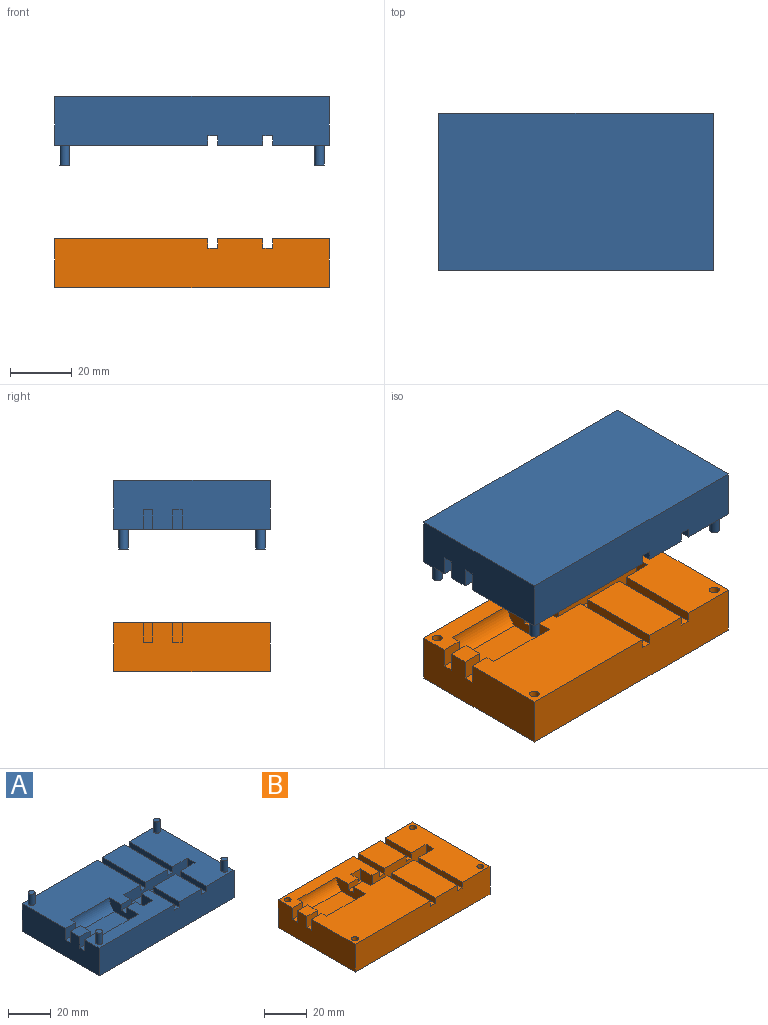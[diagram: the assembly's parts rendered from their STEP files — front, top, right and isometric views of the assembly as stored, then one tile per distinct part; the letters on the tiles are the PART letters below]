
ASSEMBLY  parts=2 mates=1
PART A: 54 faces, bbox 88.9x50.8x22.2 mm
  f0: plane 28.58x14.61mm, normal (0,0,1), area 417.3mm2, adj f9,f18,f34,f36
  f1: plane 17.15x14.61mm, normal (0,0,1), area 250.4mm2, adj f5,f6,f30,f40
  f2: plane 50.8x18.34mm, normal (0,0,1), area 866mm2, adj f5,f6,f9,f18,f29,f37,f39,f44
  f3: plane 49.61x17.15mm, normal (0,0,1), area 450.8mm2, adj f5,f6,f7,f12,f13,f14,f16,f17
  f4: plane 49.61x33.34mm, normal (0,0,1), area 1359.5mm2, adj f9,f12,f14,f15,f16,f18,f20,f23
  f5: plane 88.9x15.88mm, normal (0,-1,0), area 1391.1mm2, adj f1,f2,f3,f14,f29,f30,f31,f32
  f6: plane 35.56x12.7mm, normal (0,1,0), area 350.8mm2, adj f1,f2,f3,f7,f28,f30,f31,f32
  f7: plane 7.62x6.35mm, normal (-1,0,0), area 48.4mm2, adj f3,f6,f17,f28
  f8: plane 6.35x3.18mm, normal (0,0,1), area 20.2mm2, adj f12,f16,f25,f26
  f9: plane 88.9x15.88mm, normal (0,1,0), area 1391.1mm2, adj f0,f2,f4,f14,f29,f33,f34,f35
  f10: plane 6.74x6.35mm, normal (0,1,0), area 42.8mm2, adj f14,f19,f22,f27
  f11: plane 6.74x6.35mm, normal (0,-1,0), area 42.8mm2, adj f14,f19,f22,f27
  f12: plane 19.03x6.35mm, normal (-1,0,0), area 98.7mm2, adj f3,f4,f8,f20,f21,f22,f25,f26
  f13: plane 6.35x3.17mm, normal (1,0,0), area 14mm2, adj f3,f21,f24
  f14: plane 50.8x15.88mm, normal (-1,0,0), area 766.1mm2, adj f3,f4,f5,f9,f10,f11,f22,f23
  f15: plane 6.35x3.17mm, normal (1,0,0), area 14mm2, adj f4,f20,f23
  f16: plane 12.7x6.35mm, normal (1,0,0), area 70.6mm2, adj f3,f4,f8,f17,f18,f25,f26,f28
  f17: plane 6.35x6.35mm, normal (0,1,0), area 40.3mm2, adj f3,f7,f16,f28
  f18: plane 41.91x12.7mm, normal (0,-1,0), area 391.1mm2, adj f0,f2,f4,f16,f28,f33,f34,f35
  f19: plane 6.35x6.35mm, normal (1,0,0), area 40.3mm2, adj f10,f11,f22,f27
  f20: cylinder r=7.95mm len=25.4mm, axis (-1,0,0), area 186.8mm2, adj f4,f12,f15,f22
  f21: cylinder r=7.95mm len=25.4mm, axis (-1,0,0), area 186.8mm2, adj f3,f12,f13,f22
  f22: plane 32.14x12.7mm, normal (0,0,1), area 365.4mm2, adj f10,f11,f12,f14,f19,f20,f21,f23
  f23: plane 6.74x6.35mm, normal (0,-1,0), area 42.8mm2, adj f4,f14,f15,f22
  f24: plane 6.74x6.35mm, normal (0,1,0), area 42.8mm2, adj f3,f13,f14,f22
  f25: plane 6.35x3.18mm, normal (0,1,0), area 20.2mm2, adj f3,f8,f12,f16
  f26: plane 6.35x3.18mm, normal (0,-1,0), area 20.2mm2, adj f4,f8,f12,f16
  f27: plane 6.74x6.35mm, normal (0,0,1), area 42.8mm2, adj f10,f11,f14,f19
  f28: plane 19.05x12.7mm, normal (0,0,1), area 145.2mm2, adj f6,f7,f16,f17,f18,f43
  f29: plane 50.8x15.88mm, normal (1,0,0), area 806.5mm2, adj f2,f5,f9,f42
  f30: plane 17.15x3.18mm, normal (-1,0,0), area 54.4mm2, adj f1,f5,f6,f32
  f31: plane 17.15x3.18mm, normal (1,0,0), area 54.4mm2, adj f3,f5,f6,f32
  f32: plane 17.15x3.18mm, normal (0,0,1), area 54.4mm2, adj f5,f6,f30,f31
  f33: plane 28.58x3.18mm, normal (1,0,0), area 90.7mm2, adj f4,f9,f18,f35
  f34: plane 28.58x3.18mm, normal (-1,0,0), area 90.7mm2, adj f0,f9,f18,f35
  f35: plane 28.58x3.18mm, normal (0,0,1), area 90.7mm2, adj f9,f18,f33,f34
  f36: plane 28.58x3.18mm, normal (1,0,0), area 90.7mm2, adj f0,f9,f18,f38
  f37: plane 28.58x3.18mm, normal (-1,0,0), area 90.7mm2, adj f2,f9,f18,f38
  f38: plane 28.58x3.18mm, normal (0,0,1), area 90.7mm2, adj f9,f18,f36,f37
  f39: plane 17.15x3.18mm, normal (-1,0,0), area 54.4mm2, adj f2,f5,f6,f41
  f40: plane 17.15x3.18mm, normal (1,0,0), area 54.4mm2, adj f1,f5,f6,f41
  f41: plane 17.15x3.18mm, normal (0,0,1), area 54.4mm2, adj f5,f6,f39,f40
  f42: plane 88.9x50.8mm, normal (0,0,-1), area 4516.1mm2, adj f5,f9,f14,f29
  f43: plane 6.35x5.08mm, normal (1,0,0), area 32.3mm2, adj f6,f18,f28,f45
  f44: plane 12.7x5.08mm, normal (-1,0,0), area 64.5mm2, adj f2,f6,f18,f45
  f45: plane 22.86x5.08mm, normal (0,0,1), area 116.1mm2, adj f6,f18,f43,f44
  f46: cylinder r=1.57mm len=6.35mm, axis (0,0,-1), area 62.8mm2, adj f3,f47
  f47: plane 3.15x3.15mm, normal (0,0,1), area 7.8mm2, adj f46
  f48: cylinder r=1.57mm len=6.35mm, axis (0,0,-1), area 62.8mm2, adj f4,f49
  f49: plane 3.15x3.15mm, normal (0,0,1), area 7.8mm2, adj f48
  f50: cylinder r=1.57mm len=6.35mm, axis (0,0,-1), area 62.8mm2, adj f2,f51
  f51: plane 3.15x3.15mm, normal (0,0,1), area 7.8mm2, adj f50
  f52: cylinder r=1.57mm len=6.35mm, axis (0,0,-1), area 62.8mm2, adj f2,f53
  f53: plane 3.15x3.15mm, normal (0,0,1), area 7.8mm2, adj f52
PART B: 54 faces, bbox 88.9x50.8x15.9 mm
  f0: plane 28.58x14.61mm, normal (0,0,1), area 417.3mm2, adj f2,f15,f36,f40
  f1: plane 50.8x18.34mm, normal (0,0,1), area 865.7mm2, adj f2,f7,f15,f28,f29,f33,f37,f43
  f2: plane 88.9x15.88mm, normal (0,-1,0), area 1391.1mm2, adj f0,f1,f4,f12,f28,f36,f37,f38
  f3: plane 49.61x17.15mm, normal (0,0,1), area 450.7mm2, adj f7,f10,f12,f13,f14,f16,f17,f19
  f4: plane 49.61x33.34mm, normal (0,0,1), area 1359.4mm2, adj f2,f10,f11,f12,f14,f15,f20,f23
  f5: plane 17.15x14.61mm, normal (0,0,1), area 250.4mm2, adj f7,f29,f30,f34
  f6: plane 6.35x3.18mm, normal (0,0,1), area 20.2mm2, adj f10,f14,f24,f25
  f7: plane 88.9x15.88mm, normal (0,1,0), area 1391.1mm2, adj f1,f3,f5,f12,f28,f30,f31,f32
  f8: plane 6.74x6.35mm, normal (0,1,0), area 42.8mm2, adj f12,f18,f21,f26
  f9: plane 6.74x6.35mm, normal (0,-1,0), area 42.8mm2, adj f12,f18,f21,f26
  f10: plane 19.03x6.35mm, normal (-1,0,0), area 98.7mm2, adj f3,f4,f6,f19,f20,f21,f24,f25
  f11: plane 6.35x3.17mm, normal (1,0,0), area 14mm2, adj f4,f20,f23
  f12: plane 50.8x15.88mm, normal (-1,0,0), area 766.1mm2, adj f2,f3,f4,f7,f8,f9,f21,f22
  f13: plane 6.35x3.17mm, normal (1,0,0), area 14mm2, adj f3,f19,f22
  f14: plane 12.7x6.35mm, normal (1,0,0), area 70.6mm2, adj f3,f4,f6,f15,f17,f24,f25,f27
  f15: plane 41.91x12.7mm, normal (0,1,0), area 391.1mm2, adj f0,f1,f4,f14,f27,f36,f37,f38
  f16: plane 7.62x6.35mm, normal (-1,0,0), area 48.4mm2, adj f3,f17,f27,f29
  f17: plane 6.35x6.35mm, normal (0,-1,0), area 40.3mm2, adj f3,f14,f16,f27
  f18: plane 6.35x6.35mm, normal (1,0,0), area 40.3mm2, adj f8,f9,f21,f26
  f19: cylinder r=7.95mm len=25.4mm, axis (-1,0,0), area 186.8mm2, adj f3,f10,f13,f21
  f20: cylinder r=7.95mm len=25.4mm, axis (-1,0,0), area 186.8mm2, adj f4,f10,f11,f21
  f21: plane 32.14x12.7mm, normal (0,0,1), area 365.4mm2, adj f8,f9,f10,f12,f18,f19,f20,f22
  f22: plane 6.74x6.35mm, normal (0,-1,0), area 42.8mm2, adj f3,f12,f13,f21
  f23: plane 6.74x6.35mm, normal (0,1,0), area 42.8mm2, adj f4,f11,f12,f21
  f24: plane 6.35x3.18mm, normal (0,1,0), area 20.2mm2, adj f4,f6,f10,f14
  f25: plane 6.35x3.18mm, normal (0,-1,0), area 20.2mm2, adj f3,f6,f10,f14
  f26: plane 6.74x6.35mm, normal (0,0,1), area 42.8mm2, adj f8,f9,f12,f18
  f27: plane 19.05x12.7mm, normal (0,0,1), area 145.2mm2, adj f14,f15,f16,f17,f29,f44
  f28: plane 50.8x15.88mm, normal (1,0,0), area 806.5mm2, adj f1,f2,f7,f42
  f29: plane 35.56x12.7mm, normal (0,-1,0), area 350.8mm2, adj f1,f3,f5,f16,f27,f30,f31,f32
  f30: plane 17.15x3.18mm, normal (-1,0,0), area 54.4mm2, adj f5,f7,f29,f32
  f31: plane 17.15x3.18mm, normal (1,0,0), area 54.4mm2, adj f3,f7,f29,f32
  f32: plane 17.15x3.18mm, normal (0,0,1), area 54.4mm2, adj f7,f29,f30,f31
  f33: plane 17.15x3.18mm, normal (-1,0,0), area 54.4mm2, adj f1,f7,f29,f35
  f34: plane 17.15x3.18mm, normal (1,0,0), area 54.4mm2, adj f5,f7,f29,f35
  f35: plane 17.15x3.18mm, normal (0,0,1), area 54.4mm2, adj f7,f29,f33,f34
  f36: plane 28.58x3.18mm, normal (1,0,0), area 90.7mm2, adj f0,f2,f15,f38
  f37: plane 28.58x3.18mm, normal (-1,0,0), area 90.7mm2, adj f1,f2,f15,f38
  f38: plane 28.58x3.18mm, normal (0,0,1), area 90.7mm2, adj f2,f15,f36,f37
  f39: plane 28.58x3.18mm, normal (1,0,0), area 90.7mm2, adj f2,f4,f15,f41
  f40: plane 28.58x3.18mm, normal (-1,0,0), area 90.7mm2, adj f0,f2,f15,f41
  f41: plane 28.58x3.18mm, normal (0,0,1), area 90.7mm2, adj f2,f15,f39,f40
  f42: plane 88.9x50.8mm, normal (0,0,-1), area 4516.1mm2, adj f2,f7,f12,f28
  f43: plane 12.7x5.08mm, normal (-1,0,0), area 64.5mm2, adj f1,f15,f29,f45
  f44: plane 6.35x5.08mm, normal (1,0,0), area 32.3mm2, adj f15,f27,f29,f45
  f45: plane 22.86x5.08mm, normal (0,0,1), area 116.1mm2, adj f15,f29,f43,f44
  f46: cylinder r=1.59mm len=6.35mm, axis (0,0,1), area 63.3mm2, adj f4,f47
  f47: plane 3.18x3.18mm, normal (0,0,1), area 7.9mm2, adj f46
  f48: cylinder r=1.59mm len=6.35mm, axis (0,0,1), area 63.3mm2, adj f3,f49
  f49: plane 3.18x3.18mm, normal (0,0,1), area 7.9mm2, adj f48
  f50: cylinder r=1.59mm len=6.35mm, axis (0,0,1), area 63.3mm2, adj f1,f51
  f51: plane 3.18x3.18mm, normal (0,0,1), area 7.9mm2, adj f50
  f52: cylinder r=1.59mm len=6.35mm, axis (0,0,1), area 63.3mm2, adj f1,f53
  f53: plane 3.18x3.18mm, normal (0,0,1), area 7.9mm2, adj f52
PLACE A rot(axis=(1,0,0),180deg) t=(-59.54,-21.76,45.18)mm
PLACE B t=(-59.54,-21.76,-10.42)mm fixed
MATE slider A.f52 <-> B.f52  axis (0,0,-1) through (0.78,0.47,26.13)mm
